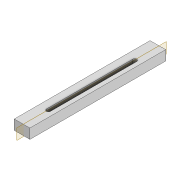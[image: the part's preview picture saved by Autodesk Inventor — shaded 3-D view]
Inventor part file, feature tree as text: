
AUTODESK INVENTOR PART (.ipt)
format: ipt  version: 2022 (Build 260153000, 153)  size: 96,256 bytes
history: native  units: mm
features: extrude x1, plane x1, sketch x1
ambient origin geometry x8: Origin, YZ Plane, XZ Plane, XY Plane, X Axis, Y Axis, Z Axis, Center Point
bodies: Solid1 (feature_tree)
feature tree (3):
  extrude  "Extrusion1"  Depth=70.0mm
  plane  "Work Plane1"
  sketch  "Sketch1"  dims[d0=3.3mm d1=70.0mm d2=10.0mm d3=10.0mm d4=20.0mm d5=20.0mm d6=6.0mm d7=8.0mm d8=0.0mm]
